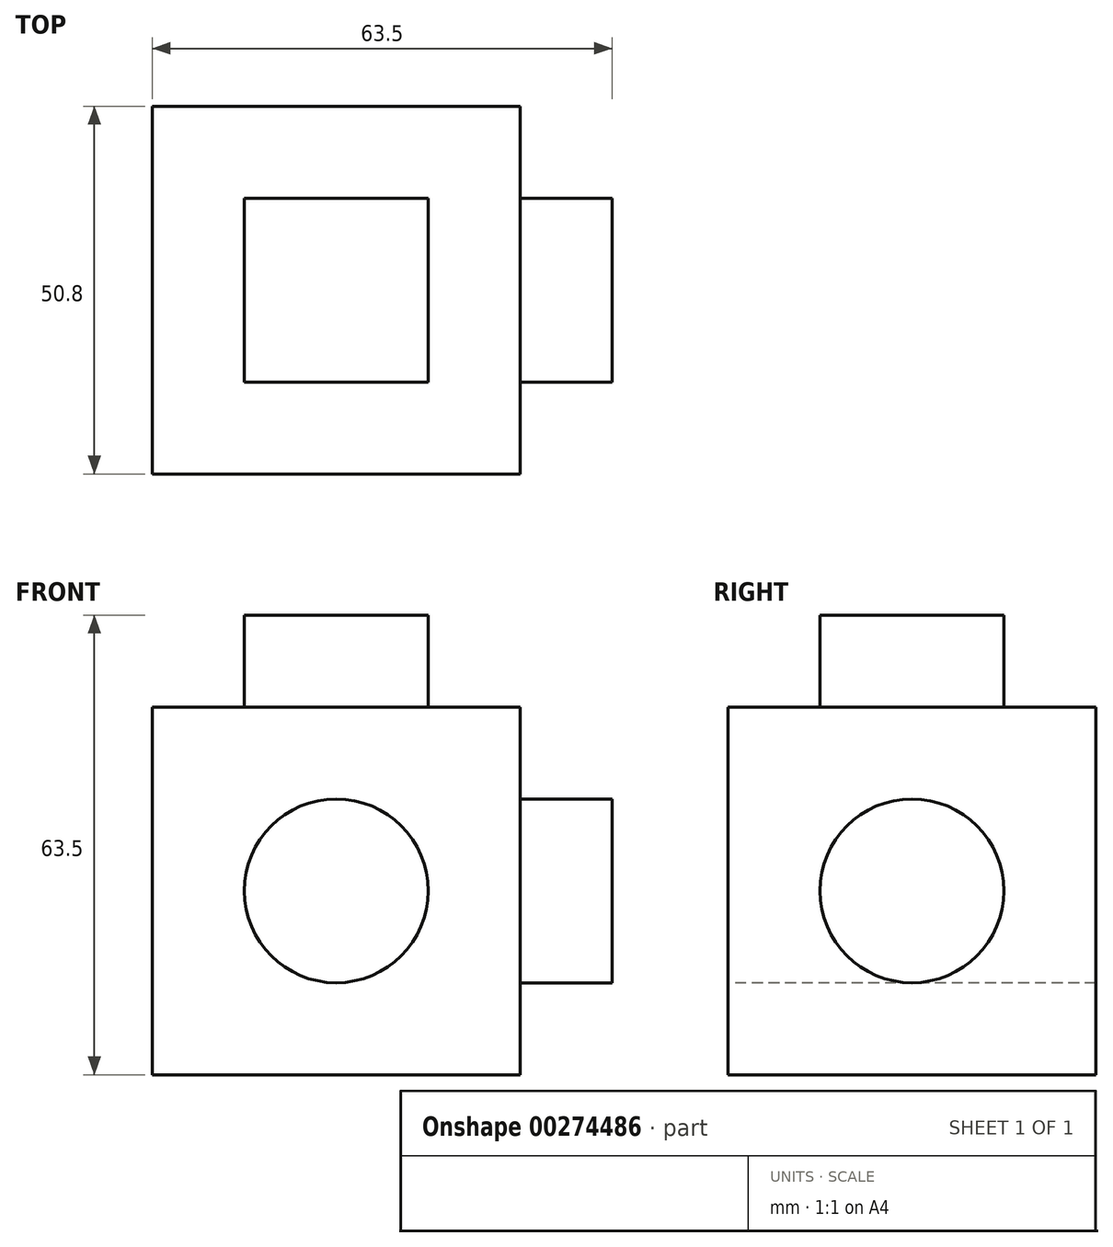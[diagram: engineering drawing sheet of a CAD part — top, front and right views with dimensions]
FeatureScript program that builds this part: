
annotation { "Feature Type Name" : "Feature", "Feature Type Description" : "" }
export const myFeature = defineFeature(function(context is Context, id is Id, definition is map)
    precondition{}
    {
        {
            var Q0;
            Q0=qCreatedBy(makeId("Front.planeOp"),FACE);
            var sketch = newSketch(context, id + "F0", { "sketchPlane" : qUnion([Q0])});
            skLineSegment(sketch, "E0.bottom", {"start": v(-25.26, 29.52) * mm, "end": v(25.54, 29.52) * mm});
            skLineSegment(sketch, "E0.top", {"start": v(-25.26, -21.28) * mm, "end": v(25.54, -21.28) * mm});
            skLineSegment(sketch, "E0.left", {"start": v(-25.26, 29.52) * mm, "end": v(-25.26, -21.28) * mm});
            skLineSegment(sketch, "E0.right", {"start": v(25.54, 29.52) * mm, "end": v(25.54, -21.28) * mm});
            skSolve(sketch);
        }
        {
            var Q0;
            Q0 = qSketchRegion(id + "F0", true);
            extrude(context, id + "F1", {"entities" : qUnion([Q0]), "depth" : 50.8 * mm});
        }
        {
            var Q0;
            Q0=makeQuery(id+"F1.opExtrude","CAP_FACE",FACE,{"disambiguationData":[OSD([sQuery(id+"F0.wireOp",EDGE,"E0.bottom"),sQuery(id+"F0.wireOp",EDGE,"E0.top"),sQuery(id+"F0.wireOp",EDGE,"E0.left"),sQuery(id+"F0.wireOp",EDGE,"E0.right")])],"isStart":false});
            var sketch = newSketch(context, id + "F2", { "sketchPlane" : qUnion([Q0])});
            skCircle(sketch, "E1", {"center": v(0.14, 4.12) * mm, "radius": 12.7 * mm});
            skSolve(sketch);
        }
        {
            var Q0;
            Q0 = qSketchRegion(id + "F2", true);
            extrude(context, id + "F3", {"entities" : qUnion([Q0]), "operationType" : NewBodyOperationType.REMOVE, "oppositeDirection" : true, "depth" : 50.8 * mm});
        }
        {
            var Q0;
            Q0=makeQuery(id+"F1.opExtrude","SWEPT_FACE",FACE,{"disambiguationData":[OSD([sQuery(id+"F0.wireOp",EDGE,"E0.bottom")])]});
            var sketch = newSketch(context, id + "F4", { "sketchPlane" : qUnion([Q0])});
            skLineSegment(sketch, "E2.bottom", {"start": v(-12.56, -12.7) * mm, "end": v(12.84, -12.7) * mm});
            skLineSegment(sketch, "E2.top", {"start": v(-12.56, -38.1) * mm, "end": v(12.84, -38.1) * mm});
            skLineSegment(sketch, "E2.left", {"start": v(-12.56, -12.7) * mm, "end": v(-12.56, -38.1) * mm});
            skLineSegment(sketch, "E2.right", {"start": v(12.84, -12.7) * mm, "end": v(12.84, -38.1) * mm});
            skSolve(sketch);
        }
        {
            var Q0;
            Q0 = qSketchRegion(id + "F4", true);
            extrude(context, id + "F5", {"entities" : qUnion([Q0]), "operationType" : NewBodyOperationType.ADD, "depth" : 12.7 * mm});
        }
        {
            var Q0;
            Q0=makeQuery(id+"F1.opExtrude","SWEPT_FACE",FACE,{"disambiguationData":[OSD([sQuery(id+"F0.wireOp",EDGE,"E0.right")])]});
            var sketch = newSketch(context, id + "F6", { "sketchPlane" : qUnion([Q0])});
            skCircle(sketch, "E3", {"center": v(-25.4, 4.12) * mm, "radius": 12.7 * mm});
            skSolve(sketch);
        }
        {
            var Q0;
            Q0 = qSketchRegion(id + "F6", true);
            extrude(context, id + "F7", {"entities" : qUnion([Q0]), "operationType" : NewBodyOperationType.ADD, "depth" : 12.7 * mm});
        }
    });
